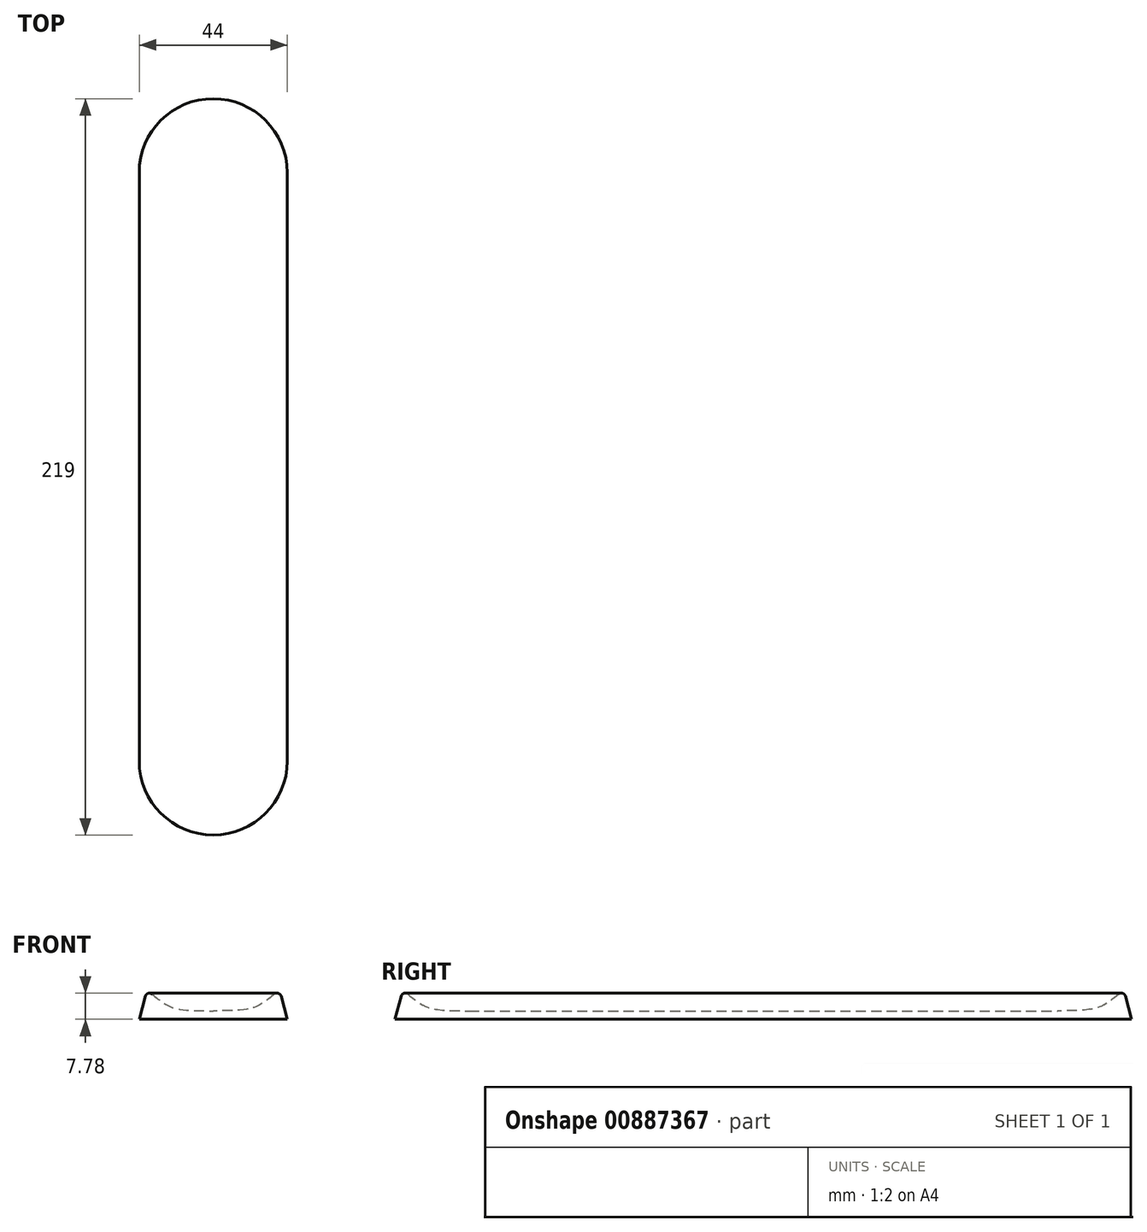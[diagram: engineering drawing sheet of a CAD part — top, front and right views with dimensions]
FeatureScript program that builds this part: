
annotation { "Feature Type Name" : "Feature", "Feature Type Description" : "" }
export const myFeature = defineFeature(function(context is Context, id is Id, definition is map)
    precondition{}
    {
        {
            var Q0;
            Q0=qCreatedBy(makeId("Front.planeOp"),FACE);
            var sketch = newSketch(context, id + "F0", { "sketchPlane" : qUnion([Q0])});
            skLineSegment(sketch, "E0", {"start": v(0, 0) * mm, "end": v(22, 0) * mm});
            skLineSegment(sketch, "E1", {"start": v(20.15, 6.9) * mm, "end": v(22, 0) * mm});
            skArc(sketch, "E2", {"start": v(20.15, 6.9) * mm, "mid": v(19.36, 7.73) * mm, "end": v(18.22, 7.5) * mm});
            skFitSpline(sketch, "E3", {"points": [v(18.22, 7.5) * mm, v(14.45, 4.68) * mm, v(0, 2.5) * mm], "startDerivative": vector(-9.93, -8.33) * mm, "endDerivative": vector(-48.36, 0) * mm});
            skLineSegment(sketch, "E4", {"start": v(18.22, 7.5) * mm, "end": v(19, 6.58) * mm, "construction": true});
            skLineSegment(sketch, "E5", {"start": v(20.15, 6.9) * mm, "end": v(19, 6.58) * mm, "construction": true});
            skLineSegment(sketch, "E6", {"start": v(0, 2.5) * mm, "end": v(0, 0) * mm});
            skSolve(sketch);
        }
        {
            var Q0;
            Q0=makeQuery(id+"F0.imprint","IMPRINT",FACE,{"disambiguationData":[TD([[makeQuery(id+"F0.imprint","IMPRINT",EDGE,{"derivedFrom":sQuery(id+"F0.wireOp",EDGE,"E0")}),1.0]])]});
            extrude(context, id + "F1", {"entities" : qUnion([Q0]), "endBound" : BoundingType.SYMMETRIC, "depth" : 175 * mm, "offsetDistance" : 25 * mm});
        }
        {
            var Q0;
            Q0=makeQuery(id+"F1.opExtrude","CAP_FACE",FACE,{"disambiguationData":[OSD([sQuery(id+"F0.wireOp",EDGE,"E0"),sQuery(id+"F0.wireOp",EDGE,"E1"),sQuery(id+"F0.wireOp",EDGE,"E2"),sQuery(id+"F0.wireOp",EDGE,"E3"),sQuery(id+"F0.wireOp",EDGE,"E6")])],"isStart":false});
            var Q1;
            Q1=makeQuery(id+"F1.opExtrude","CAP_EDGE",EDGE,{"disambiguationData":[OSD([sQuery(id+"F0.wireOp",EDGE,"E6")])],"isStart":false});
            revolve(context, id + "F2", {"operationType" : NewBodyOperationType.ADD, "surfaceOperationType" : NewSurfaceOperationType.NEW, "entities" : qUnion([Q0]), "axis" : qUnion([Q1]), "revolveType" : RevolveType.ONE_DIRECTION, "angle" : 90 * degree});
        }
        {
            var Q0;
            Q0=makeQuery(id+"F1.opExtrude","CAP_FACE",FACE,{"disambiguationData":[OSD([sQuery(id+"F0.wireOp",EDGE,"E0"),sQuery(id+"F0.wireOp",EDGE,"E1"),sQuery(id+"F0.wireOp",EDGE,"E2"),sQuery(id+"F0.wireOp",EDGE,"E3"),sQuery(id+"F0.wireOp",EDGE,"E6")])],"isStart":true});
            var Q1;
            Q1=makeQuery(id+"F1.opExtrude","CAP_EDGE",EDGE,{"disambiguationData":[OSD([sQuery(id+"F0.wireOp",EDGE,"E6")])],"isStart":true});
            revolve(context, id + "F3", {"operationType" : NewBodyOperationType.ADD, "surfaceOperationType" : NewSurfaceOperationType.NEW, "entities" : qUnion([Q0]), "axis" : qUnion([Q1]), "revolveType" : RevolveType.ONE_DIRECTION, "oppositeDirection" : true, "angle" : 90 * degree});
        }
        {
            var Q0;
            Q0=makeQuery(id+"F1.opExtrude","SWEPT_BODY",BODY,{"disambiguationData":[OSD([sQuery(id+"F0.wireOp",EDGE,"E0"),sQuery(id+"F0.wireOp",EDGE,"E1"),sQuery(id+"F0.wireOp",EDGE,"E2"),sQuery(id+"F0.wireOp",EDGE,"E3"),sQuery(id+"F0.wireOp",EDGE,"E6")])]});
            var Q1;
            {var subQ0=sQuery(id+"F0.wireOp",EDGE,"E6");var subQ1=sQuery(id+"F0.wireOp",EDGE,"E3");var subQ2=sQuery(id+"F0.wireOp",EDGE,"E2");var subQ3=sQuery(id+"F0.wireOp",EDGE,"E1");var subQ4=sQuery(id+"F0.wireOp",EDGE,"E0");Q1=makeQuery(id+"F3.boolean.opBoolean","MERGE",FACE,{"derivedFrom":[makeQuery(id+"F2.boolean.opBoolean","MERGE",FACE,{"derivedFrom":[makeQuery(id+"F1.opExtrude","SWEPT_FACE",FACE,{"disambiguationData":[OSD([subQ0])]}),makeQuery(id+"F2.opRevolve","CAP_FACE",FACE,{"disambiguationData":[OSD([subQ4,subQ3,subQ2,subQ1,subQ0])],"isStart":false})]}),makeQuery(id+"F3.opRevolve","CAP_FACE",FACE,{"disambiguationData":[OSD([subQ4,subQ3,subQ2,subQ1,subQ0])],"isStart":false})]});}
            mirror(context, id + "F4", {"operationType" : NewBodyOperationType.ADD, "entities" : qUnion([Q0]), "mirrorPlane" : qUnion([Q1])});
        }
    });
